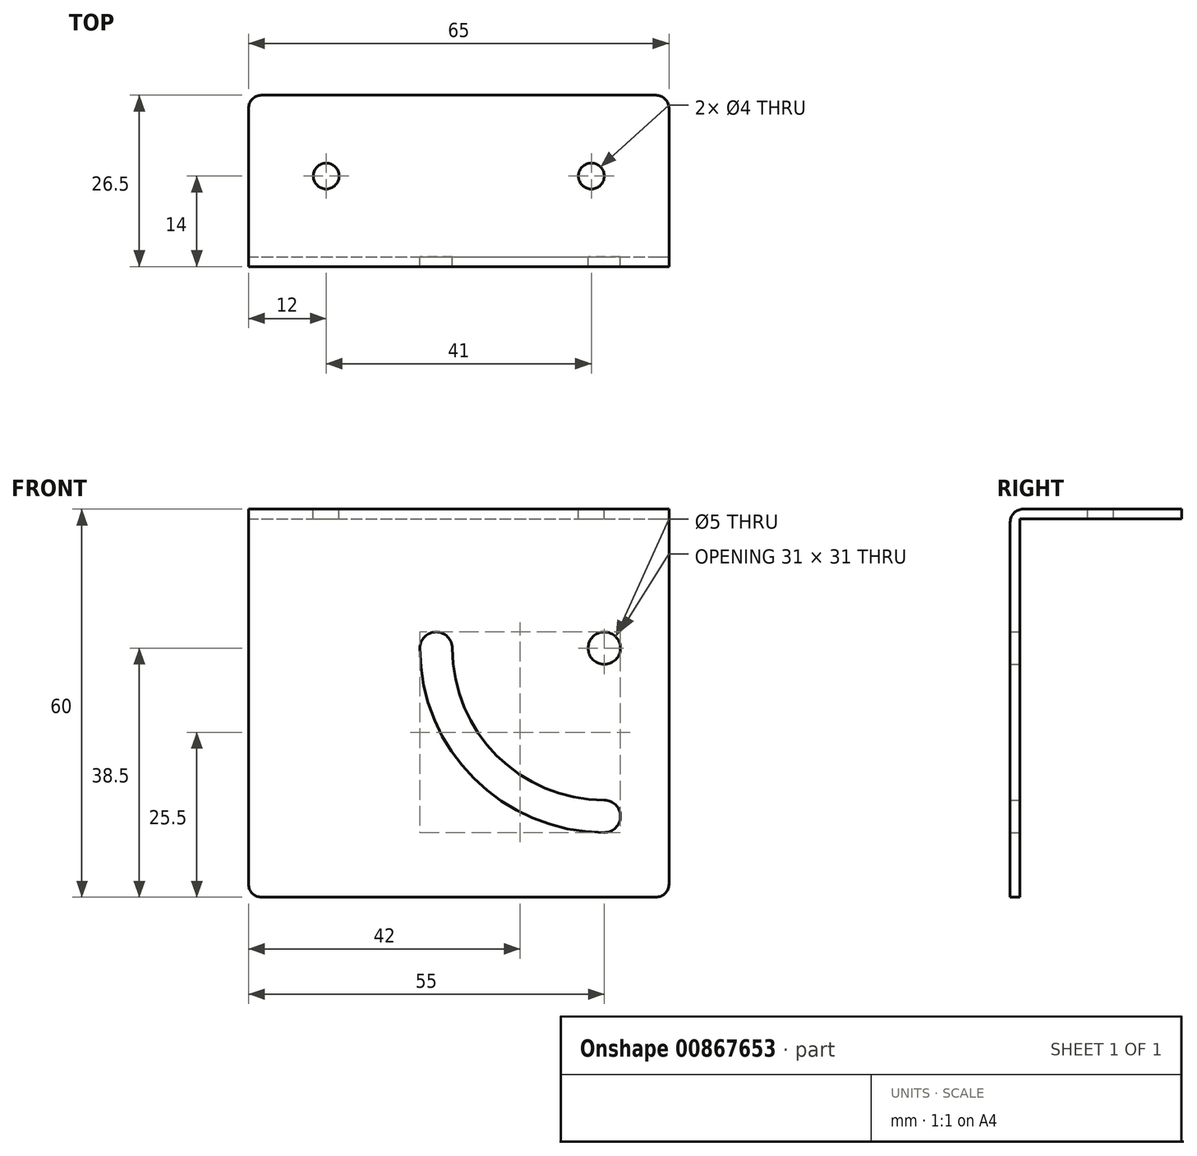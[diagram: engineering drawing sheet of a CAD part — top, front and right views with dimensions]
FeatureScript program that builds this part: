
annotation { "Feature Type Name" : "Feature", "Feature Type Description" : "" }
export const myFeature = defineFeature(function(context is Context, id is Id, definition is map)
    precondition{}
    {
        {
            var Q0;
            Q0=qCreatedBy(makeId("Front.planeOp"),FACE);
            var sketch = newSketch(context, id + "F0", { "sketchPlane" : qUnion([Q0])});
            skLineSegment(sketch, "E0.bottom", {"start": v(0, 0) * mm, "end": v(65, 0) * mm});
            skLineSegment(sketch, "E0.top", {"start": v(0, -60) * mm, "end": v(65, -60) * mm});
            skLineSegment(sketch, "E0.left", {"start": v(0, 0) * mm, "end": v(0, -60) * mm});
            skLineSegment(sketch, "E0.right", {"start": v(65, 0) * mm, "end": v(65, -60) * mm});
            skSolve(sketch);
        }
        {
            var Q0;
            Q0=makeQuery(id+"F0.imprint","IMPRINT",FACE,{"disambiguationData":[TD([[makeQuery(id+"F0.imprint","IMPRINT",EDGE,{"derivedFrom":sQuery(id+"F0.wireOp",EDGE,"E0.bottom")}),-1.0]])]});
            var sketch = newSketch(context, id + "F1", { "sketchPlane" : qUnion([Q0])});
            skCircle(sketch, "E1", {"center": v(55, -21.5) * mm, "radius": 2.5 * mm});
            skArc(sketch, "E2", {"start": v(55, -50) * mm, "mid": v(57.5, -47.5) * mm, "end": v(55, -45) * mm});
            skArc(sketch, "E3", {"start": v(31.5, -21.5) * mm, "mid": v(29, -19) * mm, "end": v(26.5, -21.5) * mm});
            skArc(sketch, "E4", {"start": v(55, -50) * mm, "mid": v(34.85, -41.65) * mm, "end": v(26.5, -21.5) * mm});
            skArc(sketch, "E5", {"start": v(55, -45) * mm, "mid": v(38.38, -38.12) * mm, "end": v(31.5, -21.5) * mm});
            skSolve(sketch);
        }
        {
            var Q0;
            Q0=makeQuery(id+"F1.imprint","IMPRINT",FACE,{"disambiguationData":[TD([[makeQuery(id+"F1.imprint","IMPRINT",EDGE,{"derivedFrom":sQuery(id+"F1.wireOp",EDGE,"E1")}),-1.0]])]});
            extrude(context, id + "F2", {"entities" : qUnion([Q0]), "depth" : 1.5 * mm, "offsetDistance" : 25 * mm});
        }
        {
            var Q0;
            Q0=qCreatedBy(makeId("Front.planeOp"),FACE);
            var sketch = newSketch(context, id + "F3", { "sketchPlane" : qUnion([Q0])});
            skLineSegment(sketch, "E6.bottom", {"start": v(0, 0) * mm, "end": v(65, 0) * mm});
            skLineSegment(sketch, "E6.top", {"start": v(0, -1.5) * mm, "end": v(65, -1.5) * mm});
            skLineSegment(sketch, "E6.left", {"start": v(0, 0) * mm, "end": v(0, -1.5) * mm});
            skLineSegment(sketch, "E6.right", {"start": v(65, 0) * mm, "end": v(65, -1.5) * mm});
            skSolve(sketch);
        }
        {
            var Q0;
            Q0 = qSketchRegion(id + "F3", true);
            extrude(context, id + "F4", {"entities" : qUnion([Q0]), "operationType" : NewBodyOperationType.ADD, "oppositeDirection" : true, "depth" : 25 * mm, "offsetDistance" : 25 * mm});
        }
        {
            var Q0;
            Q0=makeQuery(id+"F4.boolean.opBoolean","MERGE",FACE,{"derivedFrom":[makeQuery(id+"F2.opExtrude","SWEPT_FACE",FACE,{"disambiguationData":[OSD([sQuery(id+"F0.wireOp",EDGE,"E0.bottom")])]}),makeQuery(id+"F4.opExtrude","SWEPT_FACE",FACE,{"disambiguationData":[OSD([sQuery(id+"F3.wireOp",EDGE,"E6.bottom")])]})]});
            var sketch = newSketch(context, id + "F5", { "sketchPlane" : qUnion([Q0])});
            skCircle(sketch, "E7", {"center": v(12, 12.5) * mm, "radius": 2 * mm});
            skCircle(sketch, "E8", {"center": v(53, 12.5) * mm, "radius": 2 * mm});
            skSolve(sketch);
        }
        {
            var Q0;
            Q0=makeQuery(id+"F5.imprint","IMPRINT",FACE,{"disambiguationData":[TD([[makeQuery(id+"F5.imprint","IMPRINT",EDGE,{"derivedFrom":sQuery(id+"F5.wireOp",EDGE,"E8")}),1.0]])]});
            var Q1;
            Q1=makeQuery(id+"F5.imprint","IMPRINT",FACE,{"disambiguationData":[TD([[makeQuery(id+"F5.imprint","IMPRINT",EDGE,{"derivedFrom":sQuery(id+"F5.wireOp",EDGE,"E7")}),1.0]])]});
            extrude(context, id + "F6", {"entities" : qUnion([Q0, Q1]), "operationType" : NewBodyOperationType.REMOVE, "oppositeDirection" : true, "depth" : 25 * mm, "offsetDistance" : 25 * mm});
        }
        {
            var Q0;
            Q0=makeQuery(id+"F2.opExtrude","SWEPT_EDGE",EDGE,{"disambiguationData":[OSD([sQuery(id+"F0.wireOp",EDGE,"E0.top"),sQuery(id+"F0.wireOp",EDGE,"E0.right")])]});
            var Q1;
            Q1=makeQuery(id+"F4.opExtrude","CAP_EDGE",EDGE,{"disambiguationData":[OSD([sQuery(id+"F3.wireOp",EDGE,"E6.top")])],"isStart":true});
            var Q2;
            Q2=makeQuery(id+"F2.opExtrude","CAP_EDGE",EDGE,{"disambiguationData":[OSD([sQuery(id+"F0.wireOp",EDGE,"E0.bottom")])],"isStart":false});
            var Q3;
            Q3=makeQuery(id+"F2.opExtrude","SWEPT_EDGE",EDGE,{"disambiguationData":[OSD([sQuery(id+"F0.wireOp",EDGE,"E0.top"),sQuery(id+"F0.wireOp",EDGE,"E0.left")])]});
            var Q4;
            Q4=makeQuery(id+"F4.opExtrude","CAP_EDGE",EDGE,{"disambiguationData":[OSD([sQuery(id+"F3.wireOp",EDGE,"E6.left")])],"isStart":false});
            var Q5;
            Q5=makeQuery(id+"F4.opExtrude","CAP_EDGE",EDGE,{"disambiguationData":[OSD([sQuery(id+"F3.wireOp",EDGE,"E6.right")])],"isStart":false});
            fillet(context, id + "F7", {"entities" : qUnion([Q0, Q1, Q2, Q3, Q4, Q5]), "radius" : 2 * mm, "tangentPropagation" : true, "allowEdgeOverflow" : false});
        }
    });
